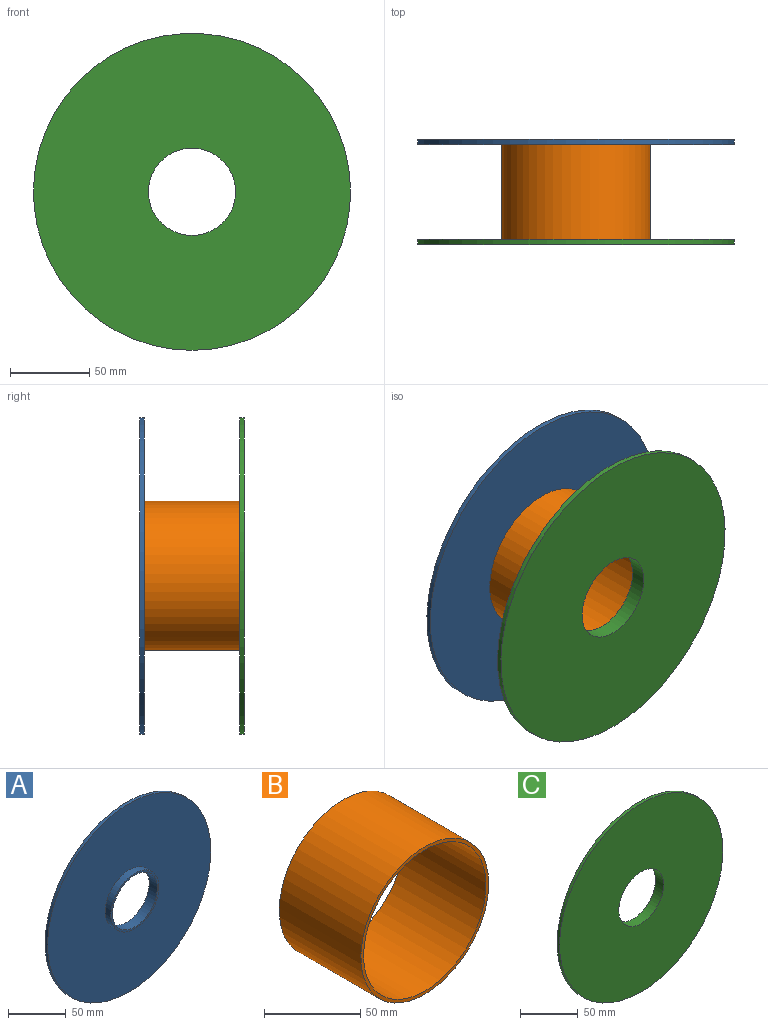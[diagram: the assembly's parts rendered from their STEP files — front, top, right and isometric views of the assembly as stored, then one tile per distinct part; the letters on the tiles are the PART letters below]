
ASSEMBLY  parts=3 mates=2
PART A: 6 faces, bbox 200x10x200 mm
  f0: cylinder r=100mm len=200mm, axis (0,1,0), area 1885mm2, adj f1,f2
  f1: plane 200x200mm, normal (0,-1,0), area 28682mm2, adj f0,f3
  f2: plane 200x200mm, normal (0,1,0), area 29040.1mm2, adj f0,f4
  f3: cylinder r=29.5mm len=59mm, axis (0,1,0), area 1297.5mm2, adj f1,f5
  f4: cylinder r=27.5mm len=55mm, axis (0,1,0), area 1727.9mm2, adj f2,f5
  f5: plane 59x59mm, normal (0,-1,0), area 358.1mm2, adj f3,f4
PART B: 4 faces, bbox 94x60x94 mm
  f0: cylinder r=45mm len=90mm, axis (0,1,0), area 16964.6mm2, adj f2,f3
  f1: cylinder r=47mm len=94mm, axis (0,1,0), area 17718.6mm2, adj f2,f3
  f2: plane 94x94mm, normal (0,-1,0), area 578.1mm2, adj f0,f1
  f3: plane 94x94mm, normal (0,1,0), area 578.1mm2, adj f0,f1
PART C: 6 faces, bbox 200x10x200 mm
  f0: cylinder r=100mm len=200mm, axis (0,-1,0), area 1885mm2, adj f1,f2
  f1: plane 200x200mm, normal (0,1,0), area 28682mm2, adj f0,f3
  f2: plane 200x200mm, normal (0,-1,0), area 29040.1mm2, adj f0,f4
  f3: cylinder r=29.5mm len=59mm, axis (0,-1,0), area 1297.5mm2, adj f1,f5
  f4: cylinder r=27.5mm len=55mm, axis (0,-1,0), area 1727.9mm2, adj f2,f5
  f5: plane 59x59mm, normal (0,1,0), area 358.1mm2, adj f3,f4
PLACE A t=(0,231,0)mm
PLACE B t=(0,228,0)mm
PLACE C t=(0,165,0)mm
MATE fastened A.f0 <-> B.f0  axis (0,-1,0) through (0,228,0)mm
MATE fastened C.f0 <-> B.f0  axis (0,1,0) through (0,168,0)mm
